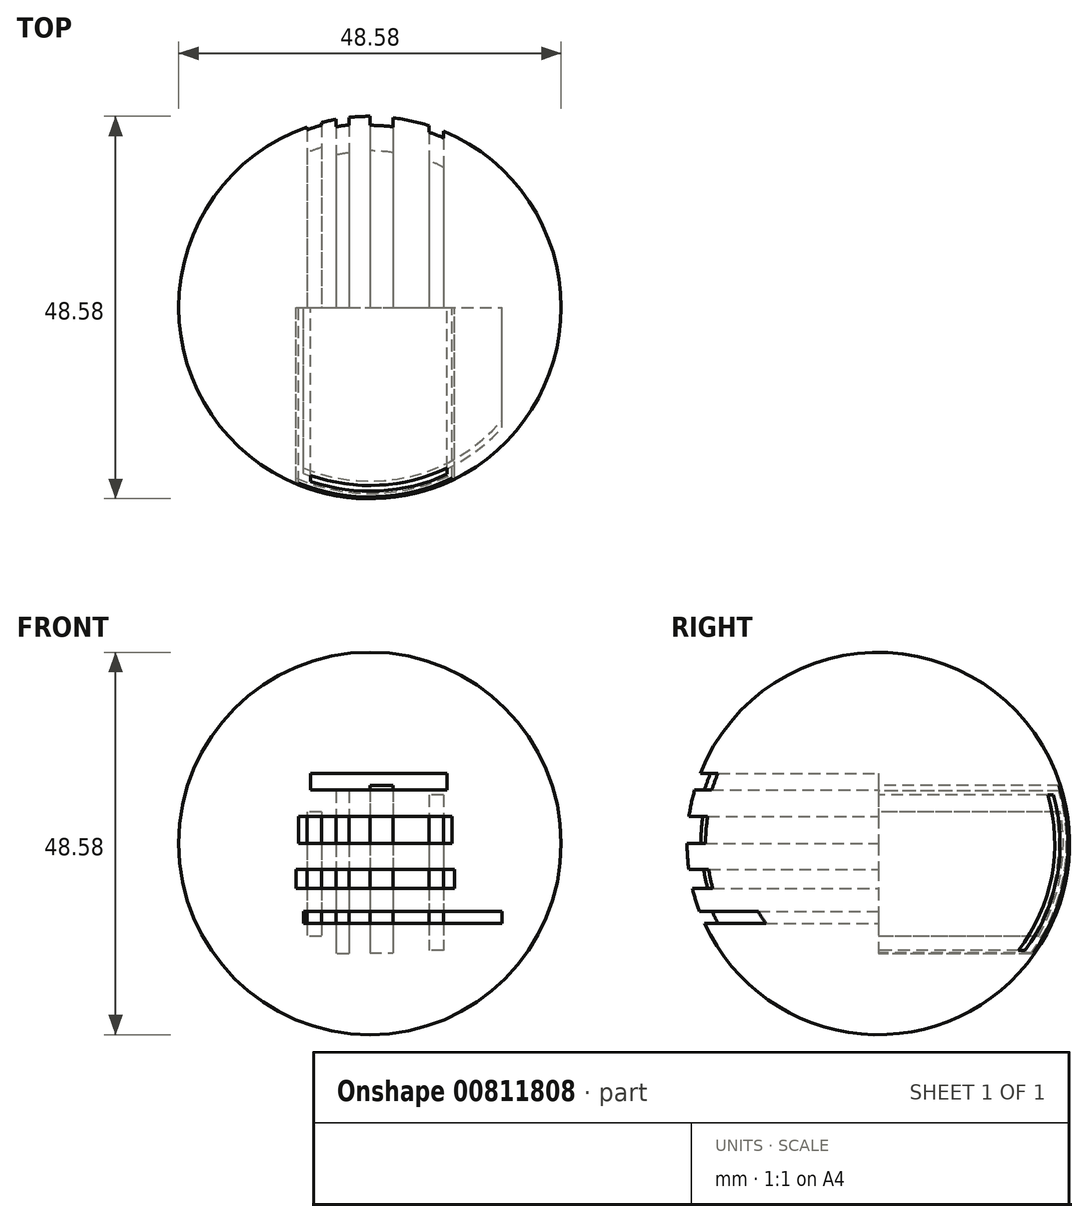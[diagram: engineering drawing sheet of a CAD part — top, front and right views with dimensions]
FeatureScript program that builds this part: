
annotation { "Feature Type Name" : "Feature", "Feature Type Description" : "" }
export const myFeature = defineFeature(function(context is Context, id is Id, definition is map)
    precondition{}
    {
        {
            var Q0;
            Q0=qCreatedBy(makeId("Front.planeOp"),FACE);
            var sketch = newSketch(context, id + "F0", { "sketchPlane" : qUnion([Q0])});
            skCircle(sketch, "E0", {"center": v(0, 0) * mm, "radius": 24.3 * mm});
            skLineSegment(sketch, "E1", {"start": v(-24.3, 0) * mm, "end": v(24.3, 0) * mm});
            skSolve(sketch);
        }
        {
            var Q0;
            {var subQ0=sQuery(id+"F0.wireOp",EDGE,"E1");Q0=makeQuery(id+"F0.imprint","IMPRINT",FACE,{"disambiguationData":[TD([[makeQuery(id+"F0.imprint","IMPRINT",EDGE,{"derivedFrom":subQ0}),1.0]])]});}
            var Q1;
            Q1=sQuery(id+"F0.wireOp",EDGE,"E1");
            revolve(context, id + "F1", {"surfaceOperationType" : NewSurfaceOperationType.NEW, "entities" : qUnion([Q0]), "axis" : qUnion([Q1]), "revolveType" : RevolveType.FULL});
        }
        {
            var Q0;
            Q0=qCreatedBy(makeId("Front.planeOp"),FACE);
            var sketch = newSketch(context, id + "F2", { "sketchPlane" : qUnion([Q0])});
            skLineSegment(sketch, "E2.bottom", {"start": v(6, 5.55) * mm, "end": v(4.49, 5.55) * mm});
            skLineSegment(sketch, "E2.top", {"start": v(6, -11.79) * mm, "end": v(4.49, -11.79) * mm});
            skLineSegment(sketch, "E2.left", {"start": v(6, 5.55) * mm, "end": v(6, -11.79) * mm});
            skLineSegment(sketch, "E2.right", {"start": v(4.49, 5.55) * mm, "end": v(4.49, -11.79) * mm});
            skLineSegment(sketch, "E3.bottom", {"start": v(0, 5.86) * mm, "end": v(-2.2, 5.86) * mm});
            skLineSegment(sketch, "E3.top", {"start": v(0, -11.79) * mm, "end": v(-2.2, -11.79) * mm});
            skLineSegment(sketch, "E3.left", {"start": v(0, 5.86) * mm, "end": v(0, -11.79) * mm});
            skLineSegment(sketch, "E3.right", {"start": v(-2.2, 5.86) * mm, "end": v(-2.2, -11.79) * mm});
            skLineSegment(sketch, "E4.bottom", {"start": v(-6.16, 4.03) * mm, "end": v(-7.99, 4.03) * mm});
            skLineSegment(sketch, "E4.top", {"start": v(-6.16, -11.79) * mm, "end": v(-7.99, -11.79) * mm});
            skLineSegment(sketch, "E4.left", {"start": v(-6.16, 4.03) * mm, "end": v(-6.16, -11.79) * mm});
            skLineSegment(sketch, "E4.right", {"start": v(-7.99, 4.03) * mm, "end": v(-7.99, -11.79) * mm});
            skLineSegment(sketch, "E5.bottom", {"start": v(8.9, 4.03) * mm, "end": v(10.72, 4.03) * mm});
            skLineSegment(sketch, "E5.top", {"start": v(8.9, -11.79) * mm, "end": v(10.72, -11.79) * mm});
            skLineSegment(sketch, "E5.left", {"start": v(8.9, 4.03) * mm, "end": v(8.9, -11.79) * mm});
            skLineSegment(sketch, "E5.right", {"start": v(10.72, 4.03) * mm, "end": v(10.72, -11.79) * mm});
            skSolve(sketch);
        }
        {
            var Q0;
            Q0=makeQuery(id+"F2.imprint","IMPRINT",FACE,{"disambiguationData":[TD([[makeQuery(id+"F2.imprint","IMPRINT",EDGE,{"derivedFrom":sQuery(id+"F2.wireOp",EDGE,"E4.bottom")}),1.0]])]});
            extrude(context, id + "F3", {"entities" : qUnion([Q0]), "operationType" : NewBodyOperationType.REMOVE, "oppositeDirection" : true, "depth" : 50.8 * mm, "offsetDistance" : 25.4 * mm});
        }
        {
            var Q0;
            Q0=qCreatedBy(makeId("Front.planeOp"),FACE);
            var sketch = newSketch(context, id + "F4", { "sketchPlane" : qUnion([Q0])});
            skLineSegment(sketch, "E6.bottom", {"start": v(0, 7.38) * mm, "end": v(2.97, 7.38) * mm});
            skLineSegment(sketch, "E6.top", {"start": v(0, -13.92) * mm, "end": v(2.97, -13.92) * mm});
            skLineSegment(sketch, "E6.left", {"start": v(0, 7.38) * mm, "end": v(0, -13.92) * mm});
            skLineSegment(sketch, "E6.right", {"start": v(2.97, 7.38) * mm, "end": v(2.97, -13.92) * mm});
            skSolve(sketch);
        }
        {
            var Q0;
            Q0=makeQuery(id+"F4.imprint","IMPRINT",FACE,{"disambiguationData":[TD([[makeQuery(id+"F4.imprint","IMPRINT",EDGE,{"derivedFrom":sQuery(id+"F4.wireOp",EDGE,"E6.bottom")}),-1.0]])]});
            var Q1;
            Q1=sQuery(id+"F4.wireOp",EDGE,"E6.left");
            var Q2;
            Q2=sQuery(id+"F4.wireOp",EDGE,"E6.right");
            var Q3;
            Q3=sQuery(id+"F4.wireOp",EDGE,"E6.top");
            var Q4;
            Q4=sQuery(id+"F4.wireOp",EDGE,"E6.bottom");
            extrude(context, id + "F5", {"entities" : qUnion([Q0]), "operationType" : NewBodyOperationType.REMOVE, "surfaceOperationType" : NewSurfaceOperationType.ADD, "surfaceEntities" : qUnion([Q1, Q2, Q3, Q4]), "oppositeDirection" : true, "depth" : 50.8 * mm, "offsetDistance" : 25.4 * mm});
        }
        {
            var Q0;
            Q0=qCreatedBy(makeId("Front.planeOp"),FACE);
            var sketch = newSketch(context, id + "F6", { "sketchPlane" : qUnion([Q0])});
            skLineSegment(sketch, "E7.bottom", {"start": v(-2.68, 6.66) * mm, "end": v(-4.3, 6.66) * mm});
            skLineSegment(sketch, "E7.top", {"start": v(-2.68, -14.02) * mm, "end": v(-4.3, -14.02) * mm});
            skLineSegment(sketch, "E7.left", {"start": v(-2.68, 6.66) * mm, "end": v(-2.68, -14.02) * mm});
            skLineSegment(sketch, "E7.right", {"start": v(-4.3, 6.66) * mm, "end": v(-4.3, -14.02) * mm});
            skSolve(sketch);
        }
        {
            var Q0;
            Q0=makeQuery(id+"F6.imprint","IMPRINT",FACE,{"disambiguationData":[TD([[makeQuery(id+"F6.imprint","IMPRINT",EDGE,{"derivedFrom":sQuery(id+"F6.wireOp",EDGE,"E7.bottom")}),1.0]])]});
            extrude(context, id + "F7", {"entities" : qUnion([Q0]), "operationType" : NewBodyOperationType.REMOVE, "oppositeDirection" : true, "depth" : 50.8 * mm, "offsetDistance" : 25.4 * mm});
        }
        {
            var Q0;
            Q0=qCreatedBy(makeId("Front.planeOp"),FACE);
            var sketch = newSketch(context, id + "F8", { "sketchPlane" : qUnion([Q0])});
            skLineSegment(sketch, "E8.bottom", {"start": v(9.35, 6.16) * mm, "end": v(7.53, 6.16) * mm});
            skLineSegment(sketch, "E8.top", {"start": v(9.35, -13.61) * mm, "end": v(7.53, -13.61) * mm});
            skLineSegment(sketch, "E8.left", {"start": v(9.35, 6.16) * mm, "end": v(9.35, -13.61) * mm});
            skLineSegment(sketch, "E8.right", {"start": v(7.53, 6.16) * mm, "end": v(7.53, -13.61) * mm});
            skSolve(sketch);
        }
        {
            var Q0;
            Q0=makeQuery(id+"F8.imprint","IMPRINT",FACE,{"disambiguationData":[TD([[makeQuery(id+"F8.imprint","IMPRINT",EDGE,{"derivedFrom":sQuery(id+"F8.wireOp",EDGE,"E8.bottom")}),1.0]])]});
            extrude(context, id + "F9", {"entities" : qUnion([Q0]), "operationType" : NewBodyOperationType.REMOVE, "oppositeDirection" : true, "depth" : 50.8 * mm, "offsetDistance" : 25.4 * mm});
        }
        {
            var Q0;
            Q0=qCreatedBy(makeId("Front.planeOp"),FACE);
            var sketch = newSketch(context, id + "F10", { "sketchPlane" : qUnion([Q0])});
            skLineSegment(sketch, "E9.bottom", {"start": v(-7.53, 8.9) * mm, "end": v(9.81, 8.9) * mm});
            skLineSegment(sketch, "E9.top", {"start": v(-7.53, 6.77) * mm, "end": v(9.81, 6.77) * mm});
            skLineSegment(sketch, "E9.left", {"start": v(-7.53, 8.9) * mm, "end": v(-7.53, 6.77) * mm});
            skLineSegment(sketch, "E9.right", {"start": v(9.81, 8.9) * mm, "end": v(9.81, 6.77) * mm});
            skSolve(sketch);
        }
        {
            var Q0;
            Q0=makeQuery(id+"F10.imprint","IMPRINT",FACE,{"disambiguationData":[TD([[makeQuery(id+"F10.imprint","IMPRINT",EDGE,{"derivedFrom":sQuery(id+"F10.wireOp",EDGE,"E9.bottom")}),-1.0]])]});
            extrude(context, id + "F11", {"entities" : qUnion([Q0]), "operationType" : NewBodyOperationType.REMOVE, "oppositeDirection" : true, "depth" : -50.8 * mm, "offsetDistance" : 25.4 * mm});
        }
        {
            var Q0;
            Q0=qCreatedBy(makeId("Front.planeOp"),FACE);
            var sketch = newSketch(context, id + "F12", { "sketchPlane" : qUnion([Q0])});
            skLineSegment(sketch, "E10.bottom", {"start": v(-9.05, 3.42) * mm, "end": v(10.42, 3.42) * mm});
            skLineSegment(sketch, "E10.top", {"start": v(-9.05, 0) * mm, "end": v(10.42, 0) * mm});
            skLineSegment(sketch, "E10.left", {"start": v(-9.05, 3.42) * mm, "end": v(-9.05, 0) * mm});
            skLineSegment(sketch, "E10.right", {"start": v(10.42, 3.42) * mm, "end": v(10.42, 0) * mm});
            skSolve(sketch);
        }
        {
            var Q0;
            Q0=makeQuery(id+"F12.imprint","IMPRINT",FACE,{"disambiguationData":[TD([[makeQuery(id+"F12.imprint","IMPRINT",EDGE,{"derivedFrom":sQuery(id+"F12.wireOp",EDGE,"E10.bottom")}),-1.0]])]});
            extrude(context, id + "F13", {"entities" : qUnion([Q0]), "operationType" : NewBodyOperationType.REMOVE, "oppositeDirection" : true, "depth" : -50.8 * mm, "offsetDistance" : 25.4 * mm});
        }
        {
            var Q0;
            Q0=qCreatedBy(makeId("Front.planeOp"),FACE);
            var sketch = newSketch(context, id + "F14", { "sketchPlane" : qUnion([Q0])});
            skLineSegment(sketch, "E11.bottom", {"start": v(-9.35, -3.27) * mm, "end": v(10.72, -3.27) * mm});
            skLineSegment(sketch, "E11.top", {"start": v(-9.35, -5.7) * mm, "end": v(10.72, -5.7) * mm});
            skLineSegment(sketch, "E11.left", {"start": v(-9.35, -3.27) * mm, "end": v(-9.35, -5.7) * mm});
            skLineSegment(sketch, "E11.right", {"start": v(10.72, -3.27) * mm, "end": v(10.72, -5.7) * mm});
            skSolve(sketch);
        }
        {
            var Q0;
            Q0=makeQuery(id+"F14.imprint","IMPRINT",FACE,{"disambiguationData":[TD([[makeQuery(id+"F14.imprint","IMPRINT",EDGE,{"derivedFrom":sQuery(id+"F14.wireOp",EDGE,"E11.bottom")}),-1.0]])]});
            extrude(context, id + "F15", {"entities" : qUnion([Q0]), "operationType" : NewBodyOperationType.REMOVE, "oppositeDirection" : true, "depth" : -50.8 * mm, "offsetDistance" : 25.4 * mm});
        }
        {
            var Q0;
            Q0=qCreatedBy(makeId("Front.planeOp"),FACE);
            var sketch = newSketch(context, id + "F16", { "sketchPlane" : qUnion([Q0])});
            skLineSegment(sketch, "E12.bottom", {"start": v(-8.44, -8.65) * mm, "end": v(16.8, -8.65) * mm});
            skLineSegment(sketch, "E12.top", {"start": v(-8.44, -10.18) * mm, "end": v(16.8, -10.18) * mm});
            skLineSegment(sketch, "E12.left", {"start": v(-8.44, -8.65) * mm, "end": v(-8.44, -10.18) * mm});
            skLineSegment(sketch, "E12.right", {"start": v(16.8, -8.65) * mm, "end": v(16.8, -10.18) * mm});
            skSolve(sketch);
        }
        {
            var Q0;
            Q0=makeQuery(id+"F16.imprint","IMPRINT",FACE,{"disambiguationData":[TD([[makeQuery(id+"F16.imprint","IMPRINT",EDGE,{"derivedFrom":sQuery(id+"F16.wireOp",EDGE,"E12.bottom")}),-1.0]])]});
            extrude(context, id + "F17", {"entities" : qUnion([Q0]), "operationType" : NewBodyOperationType.REMOVE, "oppositeDirection" : true, "depth" : -50.8 * mm, "offsetDistance" : 25.4 * mm});
        }
    });
